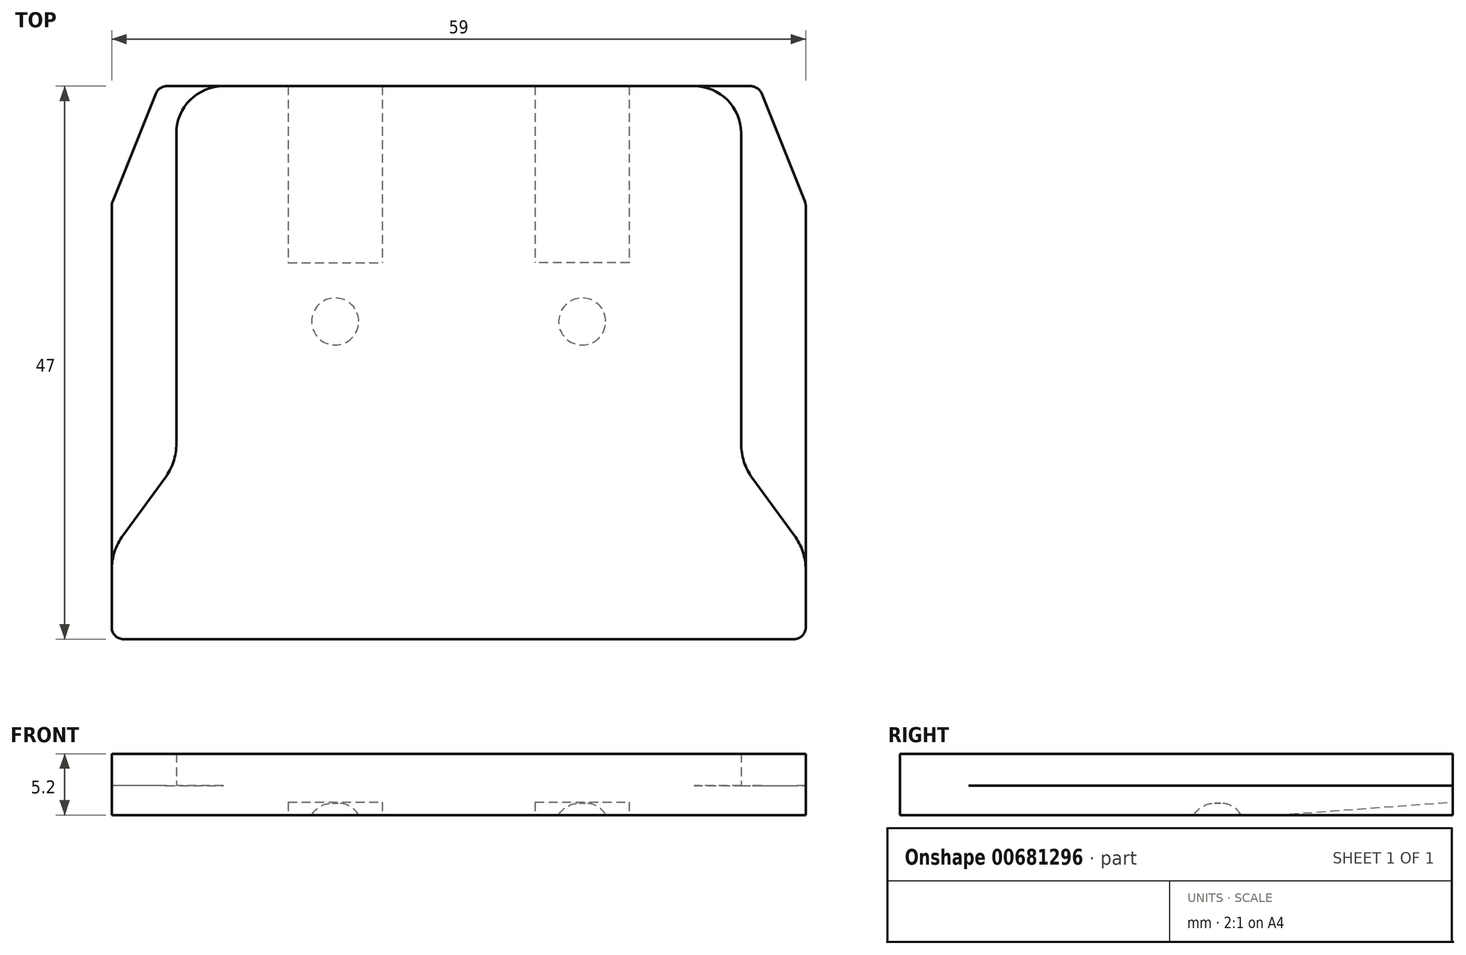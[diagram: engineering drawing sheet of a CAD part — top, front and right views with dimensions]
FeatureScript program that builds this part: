
annotation { "Feature Type Name" : "Feature", "Feature Type Description" : "" }
export const myFeature = defineFeature(function(context is Context, id is Id, definition is map)
    precondition{}
    {
        {
            var Q0;
            Q0=qCreatedBy(makeId("Top.planeOp"),FACE);
            var sketch = newSketch(context, id + "F0", { "sketchPlane" : qUnion([Q0])});
            skLineSegment(sketch, "E0.bottom", {"start": v(4, 0) * mm, "end": v(55, 0) * mm});
            skLineSegment(sketch, "E0.top", {"start": v(0, -47) * mm, "end": v(59, -47) * mm});
            skLineSegment(sketch, "E0.left", {"start": v(0, -10) * mm, "end": v(0, -47) * mm});
            skLineSegment(sketch, "E0.right", {"start": v(59, -10) * mm, "end": v(59, -47) * mm});
            skLineSegment(sketch, "E1", {"start": v(4, 0) * mm, "end": v(0, -10) * mm});
            skPoint(sketch, "E2.orphan", {"position": v(0, 0) * mm});
            skLineSegment(sketch, "E3", {"start": v(55, 0) * mm, "end": v(59, -10) * mm});
            skPoint(sketch, "E4.orphan", {"position": v(59, 0) * mm});
            skSolve(sketch);
        }
        {
            var Q0;
            Q0=makeQuery(id+"F0.imprint","IMPRINT",FACE,{"disambiguationData":[TD([[makeQuery(id+"F0.imprint","IMPRINT",EDGE,{"derivedFrom":sQuery(id+"F0.wireOp",EDGE,"E0.bottom")}),-1.0]])]});
            extrude(context, id + "F1", {"entities" : qUnion([Q0]), "depth" : 2.5 * mm, "offsetDistance" : 25 * mm});
        }
        {
            var Q0;
            Q0=makeQuery(id+"F1.opExtrude","CAP_FACE",FACE,{"disambiguationData":[OSD([sQuery(id+"F0.wireOp",EDGE,"E0.bottom"),sQuery(id+"F0.wireOp",EDGE,"E0.top"),sQuery(id+"F0.wireOp",EDGE,"E0.left"),sQuery(id+"F0.wireOp",EDGE,"E0.right"),sQuery(id+"F0.wireOp",EDGE,"E1"),sQuery(id+"F0.wireOp",EDGE,"E3")])],"isStart":false});
            var sketch = newSketch(context, id + "F2", { "sketchPlane" : qUnion([Q0])});
            skLineSegment(sketch, "E5.bottom", {"start": v(0, -47) * mm, "end": v(59, -47) * mm});
            skLineSegment(sketch, "E5.left", {"start": v(0, -47) * mm, "end": v(0, -39.5) * mm});
            skLineSegment(sketch, "E5.right", {"start": v(59, -47) * mm, "end": v(59, -39.5) * mm});
            skLineSegment(sketch, "E6.top", {"start": v(9.5, 0) * mm, "end": v(49.5, 0) * mm});
            skLineSegment(sketch, "E6.left", {"start": v(5.5, -32) * mm, "end": v(5.5, -4) * mm});
            skLineSegment(sketch, "E6.right", {"start": v(53.5, -32) * mm, "end": v(53.5, -4) * mm});
            skPoint(sketch, "E7.visualSharp", {"position": v(5.5, 0) * mm});
            skArc(sketch, "E7.filletArc", {"start": v(9.5, 0) * mm, "mid": v(6.67, -1.17) * mm, "end": v(5.5, -4) * mm});
            skPoint(sketch, "E8.visualSharp", {"position": v(53.5, 0) * mm});
            skArc(sketch, "E8.filletArc", {"start": v(53.5, -4) * mm, "mid": v(52.33, -1.17) * mm, "end": v(49.5, 0) * mm});
            skLineSegment(sketch, "E9", {"start": v(53.5, -32) * mm, "end": v(59, -39.5) * mm});
            skLineSegment(sketch, "E10", {"start": v(5.5, -32) * mm, "end": v(0, -39.5) * mm});
            skPoint(sketch, "E11.orphan", {"position": v(0, -32) * mm});
            skPoint(sketch, "E12.orphan", {"position": v(59, -32) * mm});
            skSolve(sketch);
        }
        {
            var Q0;
            Q0=makeQuery(id+"F2.imprint","IMPRINT",FACE,{"disambiguationData":[TD([[makeQuery(id+"F2.imprint","IMPRINT",EDGE,{"derivedFrom":sQuery(id+"F2.wireOp",EDGE,"E5.bottom")}),1.0]])]});
            extrude(context, id + "F3", {"entities" : qUnion([Q0]), "operationType" : NewBodyOperationType.ADD, "depth" : 2.7 * mm, "offsetDistance" : 25 * mm});
        }
        {
            var Q0;
            Q0=makeQuery(id+"F3.boolean.opBoolean","MERGE",EDGE,{"derivedFrom":[makeQuery(id+"F1.opExtrude","SWEPT_EDGE",EDGE,{"disambiguationData":[OSD([sQuery(id+"F0.wireOp",EDGE,"E0.top"),sQuery(id+"F0.wireOp",EDGE,"E0.left")])]}),makeQuery(id+"F3.opExtrude","SWEPT_EDGE",EDGE,{"disambiguationData":[OSD([sQuery(id+"F2.wireOp",EDGE,"E5.bottom"),sQuery(id+"F2.wireOp",EDGE,"E5.left")])]})]});
            var Q1;
            Q1=makeQuery(id+"F3.boolean.opBoolean","MERGE",EDGE,{"derivedFrom":[makeQuery(id+"F1.opExtrude","SWEPT_EDGE",EDGE,{"disambiguationData":[OSD([sQuery(id+"F0.wireOp",EDGE,"E0.top"),sQuery(id+"F0.wireOp",EDGE,"E0.right")])]}),makeQuery(id+"F3.opExtrude","SWEPT_EDGE",EDGE,{"disambiguationData":[OSD([sQuery(id+"F2.wireOp",EDGE,"E5.bottom"),sQuery(id+"F2.wireOp",EDGE,"E5.right")])]})]});
            var Q2;
            Q2=makeQuery(id+"F1.opExtrude","SWEPT_EDGE",EDGE,{"disambiguationData":[OSD([sQuery(id+"F0.wireOp",EDGE,"E0.bottom"),sQuery(id+"F0.wireOp",EDGE,"E1")])]});
            var Q3;
            Q3=makeQuery(id+"F1.opExtrude","SWEPT_EDGE",EDGE,{"disambiguationData":[OSD([sQuery(id+"F0.wireOp",EDGE,"E0.bottom"),sQuery(id+"F0.wireOp",EDGE,"E3")])]});
            var Q4;
            Q4=makeQuery(id+"F1.opExtrude","SWEPT_EDGE",EDGE,{"disambiguationData":[OSD([sQuery(id+"F0.wireOp",EDGE,"E0.right"),sQuery(id+"F0.wireOp",EDGE,"E3")])]});
            var Q5;
            Q5=makeQuery(id+"F1.opExtrude","SWEPT_EDGE",EDGE,{"disambiguationData":[OSD([sQuery(id+"F0.wireOp",EDGE,"E0.left"),sQuery(id+"F0.wireOp",EDGE,"E1")])]});
            fillet(context, id + "F4", {"entities" : qUnion([Q0, Q1, Q2, Q3, Q4, Q5]), "radius" : 1 * mm, "tangentPropagation" : true, "allowEdgeOverflow" : false});
        }
        {
            var Q0;
            Q0=makeQuery(id+"F3.opExtrude","SWEPT_EDGE",EDGE,{"disambiguationData":[OSD([sQuery(id+"F0.wireOp",EDGE,"E0.left"),sQuery(id+"F2.wireOp",EDGE,"E5.left"),sQuery(id+"F2.wireOp",EDGE,"E10")])]});
            var Q1;
            Q1=makeQuery(id+"F3.opExtrude","SWEPT_EDGE",EDGE,{"disambiguationData":[OSD([sQuery(id+"F0.wireOp",EDGE,"E0.right"),sQuery(id+"F2.wireOp",EDGE,"E5.right"),sQuery(id+"F2.wireOp",EDGE,"E9")])]});
            var Q2;
            Q2=makeQuery(id+"F3.opExtrude","SWEPT_EDGE",EDGE,{"disambiguationData":[OSD([sQuery(id+"F2.wireOp",EDGE,"E6.right"),sQuery(id+"F2.wireOp",EDGE,"E9")])]});
            var Q3;
            Q3=makeQuery(id+"F3.opExtrude","SWEPT_EDGE",EDGE,{"disambiguationData":[OSD([sQuery(id+"F2.wireOp",EDGE,"E6.left"),sQuery(id+"F2.wireOp",EDGE,"E10")])]});
            fillet(context, id + "F5", {"entities" : qUnion([Q0, Q1, Q2, Q3]), "radius" : 5 * mm, "tangentPropagation" : true, "allowEdgeOverflow" : false});
        }
        {
            var Q0;
            Q0=makeQuery(id+"F1.opExtrude","CAP_FACE",FACE,{"disambiguationData":[OSD([sQuery(id+"F0.wireOp",EDGE,"E0.bottom"),sQuery(id+"F0.wireOp",EDGE,"E0.top"),sQuery(id+"F0.wireOp",EDGE,"E0.left"),sQuery(id+"F0.wireOp",EDGE,"E0.right"),sQuery(id+"F0.wireOp",EDGE,"E1"),sQuery(id+"F0.wireOp",EDGE,"E3")])],"isStart":true});
            var sketch = newSketch(context, id + "F6", { "sketchPlane" : qUnion([Q0])});
            skLineSegment(sketch, "E13.bottom", {"start": v(15, 0) * mm, "end": v(23, 0) * mm});
            skLineSegment(sketch, "E13.top", {"start": v(15, 15) * mm, "end": v(23, 15) * mm});
            skLineSegment(sketch, "E13.left", {"start": v(15, 0) * mm, "end": v(15, 15) * mm});
            skLineSegment(sketch, "E13.right", {"start": v(23, 0) * mm, "end": v(23, 15) * mm});
            skLineSegment(sketch, "E14.bottom", {"start": v(44, 0) * mm, "end": v(36, 0) * mm});
            skLineSegment(sketch, "E14.top", {"start": v(44, 15) * mm, "end": v(36, 15) * mm});
            skLineSegment(sketch, "E14.left", {"start": v(44, 0) * mm, "end": v(44, 15) * mm});
            skLineSegment(sketch, "E14.right", {"start": v(36, 0) * mm, "end": v(36, 15) * mm});
            skSolve(sketch);
        }
        {
            var Q0;
            Q0=makeQuery(id+"F1.opExtrude","CAP_FACE",FACE,{"disambiguationData":[OSD([sQuery(id+"F0.wireOp",EDGE,"E0.bottom"),sQuery(id+"F0.wireOp",EDGE,"E0.top"),sQuery(id+"F0.wireOp",EDGE,"E0.left"),sQuery(id+"F0.wireOp",EDGE,"E0.right"),sQuery(id+"F0.wireOp",EDGE,"E1"),sQuery(id+"F0.wireOp",EDGE,"E3")])],"isStart":true});
            var sketch = newSketch(context, id + "F7", { "sketchPlane" : qUnion([Q0])});
            skCircle(sketch, "E15", {"center": v(19, 20) * mm, "radius": 2 * mm});
            skCircle(sketch, "E16", {"center": v(40, 20) * mm, "radius": 2 * mm});
            skSolve(sketch);
        }
        {
            var Q0;
            Q0=qSketchRegion(id+"F7",true);
            extrude(context, id + "F8", {"entities" : qUnion([Q0]), "operationType" : NewBodyOperationType.REMOVE, "oppositeDirection" : true, "depth" : 1 * mm});
        }
        {
            var Q0;
            Q0=makeQuery(id+"F6.imprint","IMPRINT",FACE,{"disambiguationData":[TD([[makeQuery(id+"F6.imprint","IMPRINT",EDGE,{"derivedFrom":sQuery(id+"F6.wireOp",EDGE,"E14.bottom")}),1.0]])]});
            var Q1;
            Q1=makeQuery(id+"F6.imprint","IMPRINT",FACE,{"disambiguationData":[TD([[makeQuery(id+"F6.imprint","IMPRINT",EDGE,{"derivedFrom":sQuery(id+"F6.wireOp",EDGE,"E13.bottom")}),1.0]])]});
            extrude(context, id + "F9", {"entities" : qUnion([Q0, Q1]), "operationType" : NewBodyOperationType.REMOVE, "oppositeDirection" : true, "depth" : 1.1 * mm});
        }
        {
            var Q0;
            Q0=makeQuery(id+"F9.boolean.opBoolean","COPY",EDGE,{"derivedFrom":makeQuery(id+"F9.opExtrude","CAP_EDGE",EDGE,{"disambiguationData":[OSD([sQuery(id+"F6.wireOp",EDGE,"E13.top")])],"isStart":false})});
            chamfer(context, id + "F10", {"entities" : qUnion([Q0]), "chamferType" : ChamferType.TWO_OFFSETS, "width1" : 1.1 * mm, "oppositeDirection" : false, "width2" : 15 * mm, "tangentPropagation" : true});
        }
        {
            var Q0;
            Q0=makeQuery(id+"F9.boolean.opBoolean","COPY",EDGE,{"derivedFrom":makeQuery(id+"F9.opExtrude","CAP_EDGE",EDGE,{"disambiguationData":[OSD([sQuery(id+"F6.wireOp",EDGE,"E14.top")])],"isStart":false})});
            chamfer(context, id + "F11", {"entities" : qUnion([Q0]), "chamferType" : ChamferType.TWO_OFFSETS, "width1" : 15 * mm, "oppositeDirection" : false, "width2" : 1.1 * mm, "tangentPropagation" : true});
        }
        {
            var Q0;
            Q0=makeQuery(id+"F8.boolean.opBoolean","COPY",EDGE,{"derivedFrom":makeQuery(id+"F8.opExtrude","CAP_EDGE",EDGE,{"disambiguationData":[OSD([sQuery(id+"F7.wireOp",EDGE,"E16")])],"isStart":false})});
            var Q1;
            Q1=makeQuery(id+"F8.boolean.opBoolean","COPY",EDGE,{"derivedFrom":makeQuery(id+"F8.opExtrude","CAP_EDGE",EDGE,{"disambiguationData":[OSD([sQuery(id+"F7.wireOp",EDGE,"E15")])],"isStart":false})});
            fillet(context, id + "F12", {"entities" : qUnion([Q0, Q1]), "radius" : 2 * mm, "tangentPropagation" : true, "allowEdgeOverflow" : false});
        }
    });
